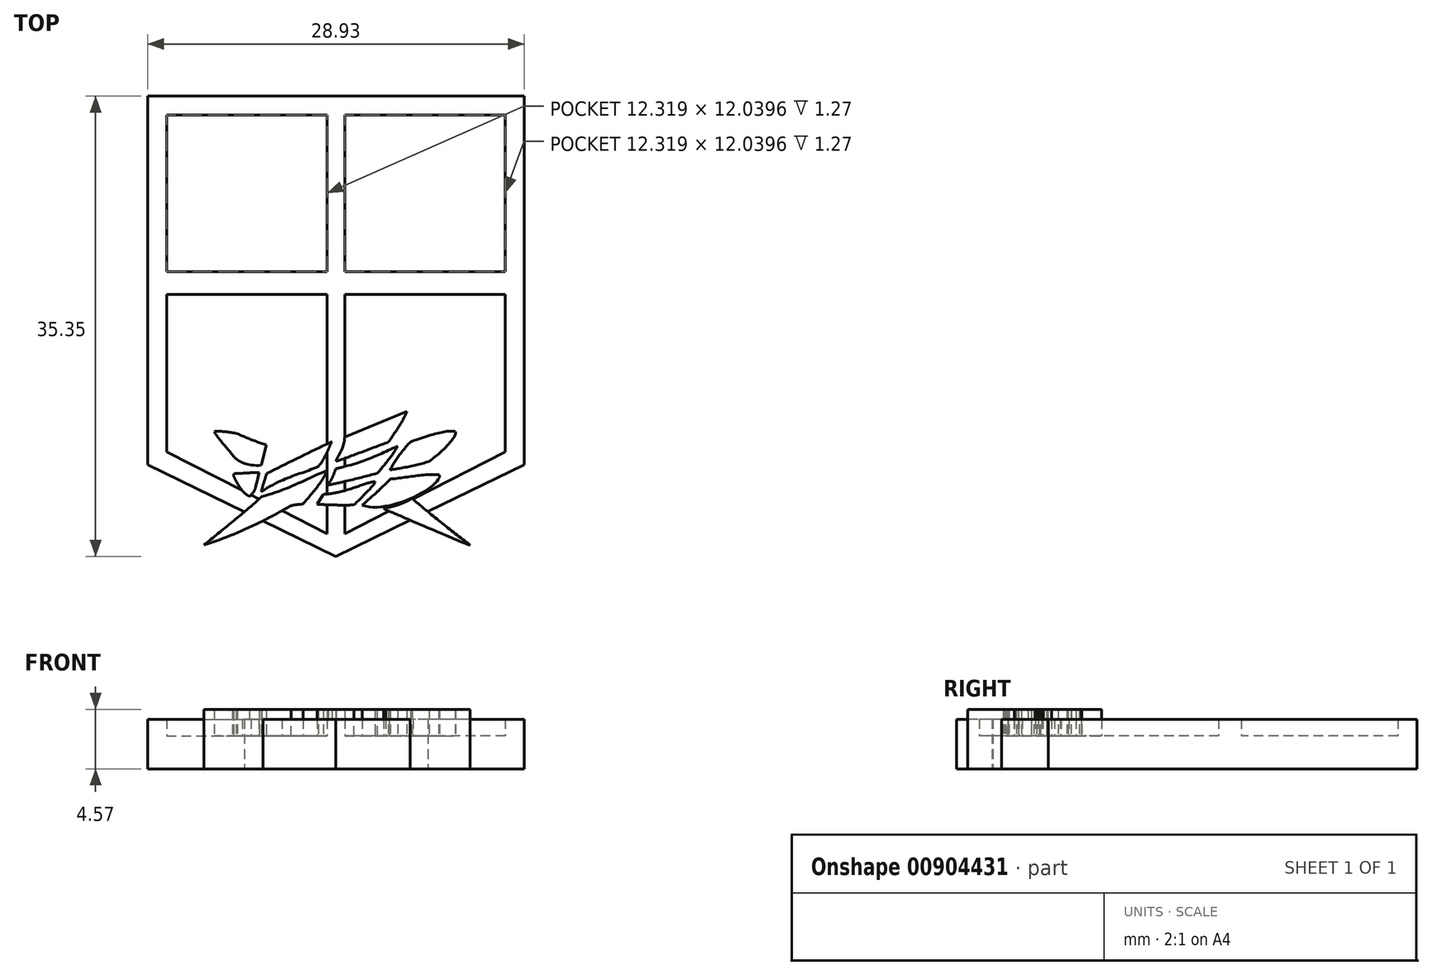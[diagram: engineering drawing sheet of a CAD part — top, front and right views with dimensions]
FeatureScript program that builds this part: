
annotation { "Feature Type Name" : "Feature", "Feature Type Description" : "" }
export const myFeature = defineFeature(function(context is Context, id is Id, definition is map)
    precondition{}
    {
        {
            var Q0;
            Q0=qCreatedBy(makeId("Top.planeOp"),FACE);
            var sketch = newSketch(context, id + "F0", { "sketchPlane" : qUnion([Q0])});
            skLineSegment(sketch, "E0", {"start": v(1.06, 6.16) * mm, "end": v(1.06, 44.26) * mm});
            skLineSegment(sketch, "E1", {"start": v(-13.4, 41.58) * mm, "end": v(-13.4, 13.28) * mm});
            skLineSegment(sketch, "E2", {"start": v(-13.4, 13.28) * mm, "end": v(1.06, 6.23) * mm});
            skLineSegment(sketch, "E3", {"start": v(-13.4, 41.58) * mm, "end": v(1.06, 41.58) * mm});
            skLineSegment(sketch, "E4", {"start": v(-11.95, 28.1) * mm, "end": v(0.37, 28.1) * mm});
            skLineSegment(sketch, "E5", {"start": v(0.37, 28.1) * mm, "end": v(0.37, 40.14) * mm});
            skLineSegment(sketch, "E6", {"start": v(0.37, 40.14) * mm, "end": v(-11.95, 40.14) * mm});
            skLineSegment(sketch, "E7", {"start": v(-11.95, 40.14) * mm, "end": v(-11.95, 28.1) * mm});
            skLineSegment(sketch, "E8", {"start": v(-11.95, 26.36) * mm, "end": v(0.37, 26.36) * mm});
            skLineSegment(sketch, "E9", {"start": v(-11.95, 26.36) * mm, "end": v(-11.95, 14.25) * mm});
            skLineSegment(sketch, "E10", {"start": v(-11.95, 14.25) * mm, "end": v(0.37, 7.97) * mm});
            skLineSegment(sketch, "E11", {"start": v(0.37, 26.36) * mm, "end": v(0.37, 7.97) * mm});
            skLineSegment(sketch, "E12.MirrorCS", {"start": v(14.08, 26.36) * mm, "end": v(1.76, 26.36) * mm});
            skLineSegment(sketch, "E13.MirrorCS", {"start": v(14.08, 26.36) * mm, "end": v(14.08, 14.25) * mm});
            skLineSegment(sketch, "E14.MirrorCS", {"start": v(14.08, 14.25) * mm, "end": v(1.76, 7.97) * mm});
            skLineSegment(sketch, "E15.MirrorCS", {"start": v(1.76, 26.36) * mm, "end": v(1.76, 7.97) * mm});
            skLineSegment(sketch, "E16.MirrorCS", {"start": v(1.76, 28.1) * mm, "end": v(1.76, 40.14) * mm});
            skLineSegment(sketch, "E17.MirrorCS", {"start": v(14.08, 40.14) * mm, "end": v(14.08, 28.1) * mm});
            skLineSegment(sketch, "E18.MirrorCS", {"start": v(14.08, 28.1) * mm, "end": v(1.76, 28.1) * mm});
            skLineSegment(sketch, "E19.MirrorCS", {"start": v(1.76, 40.14) * mm, "end": v(14.08, 40.14) * mm});
            skLineSegment(sketch, "E20.MirrorCS", {"start": v(15.53, 41.58) * mm, "end": v(1.06, 41.58) * mm});
            skLineSegment(sketch, "E21.MirrorCS", {"start": v(15.53, 41.58) * mm, "end": v(15.53, 13.28) * mm});
            skLineSegment(sketch, "E22.MirrorCS", {"start": v(15.53, 13.28) * mm, "end": v(1.06, 6.23) * mm});
            skFitSpline(sketch, "E23", {"points": [v(-4.64, 10.81) * mm, v(-9.06, 7.1) * mm], "startDerivative": vector(-4.08, -3.8) * mm, "endDerivative": vector(-4.43, -3.76) * mm});
            skFitSpline(sketch, "E24", {"points": [v(-9.06, 7.1) * mm, v(-2.38, 10.11) * mm], "startDerivative": vector(9.26, 3) * mm, "endDerivative": vector(4.95, 2.67) * mm});
            skFitSpline(sketch, "E25", {"points": [v(-2.38, 10.11) * mm, v(-1.47, 10.25) * mm], "startDerivative": vector(0.83, 0.32) * mm, "endDerivative": vector(0.9, 0.14) * mm});
            skFitSpline(sketch, "E26", {"points": [v(0.37, 12.77) * mm, v(-1.47, 10.25) * mm], "startDerivative": vector(-1.12, -2.58) * mm, "endDerivative": vector(-1.78, -2.06) * mm});
            skFitSpline(sketch, "E27", {"points": [v(0.37, 12.82) * mm, v(-4.64, 10.81) * mm], "startDerivative": vector(-5.01, -2) * mm, "endDerivative": vector(-6.37, -1.72) * mm});
            skFitSpline(sketch, "E28", {"points": [v(4.9, 9.8) * mm, v(11.38, 7.08) * mm], "startDerivative": vector(6.47, -2.73) * mm, "endDerivative": vector(1.76, -0.58) * mm});
            skFitSpline(sketch, "E29", {"points": [v(4.75, 9.93) * mm, v(4.9, 9.8) * mm], "startDerivative": vector(0.07, -0.18) * mm, "endDerivative": vector(0.18, -0.09) * mm});
            skFitSpline(sketch, "E30", {"points": [v(11.38, 7.08) * mm, v(6.92, 10.68) * mm], "startDerivative": vector(-4.53, 3.54) * mm, "endDerivative": vector(-4.26, 3.7) * mm});
            skFitSpline(sketch, "E31", {"points": [v(6.92, 10.68) * mm, v(4.75, 9.93) * mm], "startDerivative": vector(-1.87, -0.96) * mm, "endDerivative": vector(-3.66, -0.55) * mm});
            skFitSpline(sketch, "E32", {"points": [v(0.09, 10.99) * mm, v(4.08, 11.96) * mm], "startDerivative": vector(5.72, 0.35) * mm, "endDerivative": vector(2.47, 0.08) * mm});
            skFitSpline(sketch, "E33", {"points": [v(4.08, 11.96) * mm, v(2.45, 10.17) * mm], "startDerivative": vector(0.16, -0.43) * mm, "endDerivative": vector(-1.8, -1.78) * mm});
            skFitSpline(sketch, "E34", {"points": [v(2.45, 10.17) * mm, v(-0.38, 10.23) * mm], "startDerivative": vector(-2.79, -0.04) * mm, "endDerivative": vector(-2.94, 0.22) * mm});
            skFitSpline(sketch, "E35", {"points": [v(-0.38, 10.23) * mm, v(0.09, 10.99) * mm], "startDerivative": vector(0.46, 0.76) * mm, "endDerivative": vector(0.46, 0.76) * mm});
            skFitSpline(sketch, "E36", {"points": [v(5.26, 12.17) * mm, v(3.08, 10.15) * mm], "startDerivative": vector(-2.05, -2.08) * mm, "endDerivative": vector(-2.26, -1.98) * mm});
            skFitSpline(sketch, "E37", {"points": [v(3.08, 10.15) * mm, v(9, 12.28) * mm], "startDerivative": vector(5.82, -2.02) * mm, "endDerivative": vector(1.16, 2.93) * mm});
            skFitSpline(sketch, "E38", {"points": [v(9, 12.28) * mm, v(8.97, 12.5) * mm], "startDerivative": vector(0.06, 0.33) * mm, "endDerivative": vector(-0.17, 0.25) * mm});
            skFitSpline(sketch, "E39", {"points": [v(8.97, 12.5) * mm, v(5.26, 12.17) * mm], "startDerivative": vector(-3.8, 0.2) * mm, "endDerivative": vector(-3.7, -0.3) * mm});
            skFitSpline(sketch, "E40", {"points": [v(1.04, 12.95) * mm, v(0.5, 11.72) * mm], "startDerivative": vector(-0.31, -1.27) * mm, "endDerivative": vector(-0.75, -1.39) * mm});
            skFitSpline(sketch, "E41", {"points": [v(0.5, 11.72) * mm, v(4.26, 12.62) * mm], "startDerivative": vector(0.28, -0.12) * mm, "endDerivative": vector(3.72, 1.03) * mm});
            skFitSpline(sketch, "E42", {"points": [v(4.26, 12.62) * mm, v(5.81, 14.7) * mm], "startDerivative": vector(1.64, 2) * mm, "endDerivative": vector(1.44, 2.47) * mm});
            skFitSpline(sketch, "E43", {"points": [v(5.81, 14.7) * mm, v(1.04, 12.95) * mm], "startDerivative": vector(-5.12, -2.36) * mm, "endDerivative": vector(-6.9, -1.61) * mm});
            skFitSpline(sketch, "E44", {"points": [v(-4.82, 12.65) * mm, v(-5.57, 10.83) * mm], "startDerivative": vector(-1.33, -4.72) * mm, "endDerivative": vector(-1.62, -1.8) * mm});
            skFitSpline(sketch, "E45", {"points": [v(-5.57, 10.83) * mm, v(-6.8, 12.4) * mm], "startDerivative": vector(-2.19, 1.15) * mm, "endDerivative": vector(-0.4, 0.82) * mm});
            skFitSpline(sketch, "E46", {"points": [v(-6.8, 12.4) * mm, v(-6.6, 12.6) * mm], "startDerivative": vector(-0.17, 0.4) * mm, "endDerivative": vector(0.28, -0.03) * mm});
            skFitSpline(sketch, "E47", {"points": [v(-6.6, 12.6) * mm, v(-4.82, 12.65) * mm], "startDerivative": vector(3.8, 0.1) * mm, "endDerivative": vector(0.27, -0.15) * mm});
            skFitSpline(sketch, "E48", {"points": [v(5.21, 12.87) * mm, v(6.8, 15.01) * mm], "startDerivative": vector(1.32, 2.27) * mm, "endDerivative": vector(1.98, 2) * mm});
            skFitSpline(sketch, "E49", {"points": [v(6.8, 15.01) * mm, v(10.23, 15.81) * mm], "startDerivative": vector(4.76, 1.85) * mm, "endDerivative": vector(1.34, -0.46) * mm});
            skFitSpline(sketch, "E50", {"points": [v(5.21, 12.87) * mm, v(8.22, 13.53) * mm], "startDerivative": vector(2.8, 0.45) * mm, "endDerivative": vector(2.88, 1.03) * mm});
            skFitSpline(sketch, "E51", {"points": [v(8.22, 13.53) * mm, v(10.23, 15.81) * mm], "startDerivative": vector(0.67, 0.26) * mm, "endDerivative": vector(-0.9, 1.27) * mm});
            skFitSpline(sketch, "E52", {"points": [v(-4.26, 12.59) * mm, v(0.75, 15.04) * mm], "startDerivative": vector(4.98, 2.48) * mm, "endDerivative": vector(5.02, 2.41) * mm});
            skFitSpline(sketch, "E53", {"points": [v(0.75, 15.04) * mm, v(-0.28, 13.13) * mm], "startDerivative": vector(-0.88, -1.85) * mm, "endDerivative": vector(-1.56, -1.86) * mm});
            skFitSpline(sketch, "E54", {"points": [v(-0.28, 13.13) * mm, v(-4.67, 11.2) * mm], "startDerivative": vector(-4.4, -1.94) * mm, "endDerivative": vector(-5.42, -3.53) * mm});
            skFitSpline(sketch, "E55", {"points": [v(-4.67, 11.2) * mm, v(-4.26, 12.59) * mm], "startDerivative": vector(0.35, 1.39) * mm, "endDerivative": vector(0.43, 1.4) * mm});
            skFitSpline(sketch, "E56", {"points": [v(1.75, 15.4) * mm, v(6.53, 17.36) * mm], "startDerivative": vector(4.78, 1.96) * mm, "endDerivative": vector(4.78, 1.96) * mm});
            skFitSpline(sketch, "E57", {"points": [v(6.53, 17.36) * mm, v(5.1, 15) * mm], "startDerivative": vector(-1.06, -2.45) * mm, "endDerivative": vector(-1.56, -2.27) * mm});
            skFitSpline(sketch, "E58", {"points": [v(5.1, 15) * mm, v(1.07, 13.54) * mm], "startDerivative": vector(-4.03, -1.47) * mm, "endDerivative": vector(-0.26, 0.09) * mm});
            skFitSpline(sketch, "E59", {"points": [v(1.07, 13.54) * mm, v(1.75, 15.4) * mm], "startDerivative": vector(0.27, 1.25) * mm, "endDerivative": vector(0.4, 3.51) * mm});
            skFitSpline(sketch, "E60", {"points": [v(-8.27, 15.8) * mm, v(-6.88, 14.02) * mm], "startDerivative": vector(0, -0.57) * mm, "endDerivative": vector(1.37, -1.8) * mm});
            skFitSpline(sketch, "E61", {"points": [v(-6.88, 14.02) * mm, v(-4.65, 13.23) * mm], "startDerivative": vector(0.3, -0.28) * mm, "endDerivative": vector(4.86, 0.4) * mm});
            skFitSpline(sketch, "E62", {"points": [v(-4.65, 13.23) * mm, v(-4.28, 14.79) * mm], "startDerivative": vector(0.38, 1.56) * mm, "endDerivative": vector(0.38, 1.56) * mm});
            skFitSpline(sketch, "E63", {"points": [v(-4.28, 14.79) * mm, v(-6.51, 15.65) * mm], "startDerivative": vector(-2.37, 0.7) * mm, "endDerivative": vector(-2.1, 0.9) * mm});
            skFitSpline(sketch, "E64", {"points": [v(-6.51, 15.65) * mm, v(-8.27, 15.8) * mm], "startDerivative": vector(-2.53, 0.5) * mm, "endDerivative": vector(-0.34, -0.26) * mm});
            skLineSegment(sketch, "E65", {"start": v(-4.04, 15.96) * mm, "end": v(-4.15, 15.37) * mm});
            skSolve(sketch);
        }
        {
            var Q0;
            Q0=makeQuery(id+"F0.imprint","IMPRINT",FACE,{"disambiguationData":[TD([[makeQuery(id+"F0.imprint","IMPRINT",EDGE,{"derivedFrom":sQuery(id+"F0.wireOp",EDGE,"E12.MirrorCS")}),-1.0]])]});
            var Q1;
            Q1=makeQuery(id+"F0.imprint","IMPRINT",FACE,{"disambiguationData":[TD([[makeQuery(id+"F0.imprint","IMPRINT",EDGE,{"derivedFrom":sQuery(id+"F0.wireOp",EDGE,"E1")}),1.0]])]});
            var Q2;
            {var subQ0=sQuery(id+"F0.wireOp",EDGE,"E11");var subQ1=sQuery(id+"F0.wireOp",EDGE,"E10");var subQ2=makeQuery(id+"F0.imprint","INTERSECT",VERTEX,{"derivedFrom":[subQ1,subQ0]});Q2=makeQuery(id+"F0.imprint","IMPRINT",FACE,{"disambiguationData":[TD([[makeQuery(id+"F0.imprint","IMPRINT",EDGE,{"disambiguationData":[TD([[subQ2,1.0]])],"derivedFrom":subQ1}),-1.0]])]});}
            var Q3;
            {var subQ5=sQuery(id+"F0.wireOp",EDGE,"E14.MirrorCS");var subQ7=sQuery(id+"F0.wireOp",EDGE,"E15.MirrorCS");var subQ8=makeQuery(id+"F0.imprint","INTERSECT",VERTEX,{"derivedFrom":[subQ5,subQ7]});Q3=makeQuery(id+"F0.imprint","IMPRINT",FACE,{"disambiguationData":[TD([[makeQuery(id+"F0.imprint","IMPRINT",EDGE,{"disambiguationData":[TD([[subQ8,1.0]])],"derivedFrom":subQ5}),1.0]])]});}
            var Q4;
            {var subQ0=sQuery(id+"F0.wireOp",EDGE,"E32");var subQ1=sQuery(id+"F0.wireOp",EDGE,"E0");var subQ2=makeQuery(id+"F0.imprint","INTERSECT",VERTEX,{"derivedFrom":[subQ1,subQ0]});Q4=makeQuery(id+"F0.imprint","IMPRINT",FACE,{"disambiguationData":[TD([[makeQuery(id+"F0.imprint","IMPRINT",EDGE,{"disambiguationData":[TD([[subQ2,-1.0]])],"derivedFrom":subQ1}),-1.0]])]});}
            extrude(context, id + "F1", {"entities" : qUnion([Q0, Q1, Q2, Q3, Q4]), "flatOperationType" : FlatOperationType.REMOVE, "depth" : 3.8 * mm, "offsetDistance" : 25.4 * mm, "domain" : OperationDomain.MODEL});
        }
        {
            var Q0;
            Q0=makeQuery(id+"F0.imprint","IMPRINT",FACE,{"disambiguationData":[TD([[makeQuery(id+"F0.imprint","IMPRINT",EDGE,{"derivedFrom":sQuery(id+"F0.wireOp",EDGE,"E4")}),1.0]])]});
            var Q1;
            Q1=makeQuery(id+"F0.imprint","IMPRINT",FACE,{"disambiguationData":[TD([[makeQuery(id+"F0.imprint","IMPRINT",EDGE,{"derivedFrom":sQuery(id+"F0.wireOp",EDGE,"E8")}),-1.0]])]});
            var Q2;
            Q2=makeQuery(id+"F0.imprint","IMPRINT",FACE,{"disambiguationData":[TD([[makeQuery(id+"F0.imprint","IMPRINT",EDGE,{"derivedFrom":sQuery(id+"F0.wireOp",EDGE,"E12.MirrorCS")}),1.0]])]});
            var Q3;
            Q3=makeQuery(id+"F0.imprint","IMPRINT",FACE,{"disambiguationData":[TD([[makeQuery(id+"F0.imprint","IMPRINT",EDGE,{"derivedFrom":sQuery(id+"F0.wireOp",EDGE,"E16.MirrorCS")}),-1.0]])]});
            var Q4;
            {var subQ4=sQuery(id+"F0.wireOp",EDGE,"E25");Q4=makeQuery(id+"F0.imprint","IMPRINT",FACE,{"disambiguationData":[TD([[makeQuery(id+"F0.imprint","IMPRINT",EDGE,{"derivedFrom":subQ4}),-1.0]])]});}
            extrude(context, id + "F2", {"entities" : qUnion([Q0, Q1, Q2, Q3, Q4]), "operationType" : NewBodyOperationType.ADD, "flatOperationType" : FlatOperationType.REMOVE, "depth" : 2.54 * mm, "offsetDistance" : 25.4 * mm, "domain" : OperationDomain.MODEL});
        }
        {
            var Q0;
            {var subQ0=sQuery(id+"F0.wireOp",EDGE,"E25");Q0=makeQuery(id+"F0.imprint","IMPRINT",FACE,{"disambiguationData":[TD([[makeQuery(id+"F0.imprint","IMPRINT",EDGE,{"derivedFrom":subQ0}),1.0]])]});}
            var Q1;
            {var subQ0=sQuery(id+"F0.wireOp",EDGE,"E23");var subQ1=sQuery(id+"F0.wireOp",EDGE,"E2");var subQ2=makeQuery(id+"F0.imprint","INTERSECT",VERTEX,{"derivedFrom":[subQ1,subQ0]});Q1=makeQuery(id+"F0.imprint","IMPRINT",FACE,{"disambiguationData":[TD([[makeQuery(id+"F0.imprint","IMPRINT",EDGE,{"disambiguationData":[TD([[subQ2,-1.0]])],"derivedFrom":subQ1}),1.0]])]});}
            var Q2;
            {var subQ0=sQuery(id+"F0.wireOp",EDGE,"E23");var subQ1=sQuery(id+"F0.wireOp",EDGE,"E2");var subQ2=makeQuery(id+"F0.imprint","INTERSECT",VERTEX,{"derivedFrom":[subQ1,subQ0]});Q2=makeQuery(id+"F0.imprint","IMPRINT",FACE,{"disambiguationData":[TD([[makeQuery(id+"F0.imprint","IMPRINT",EDGE,{"disambiguationData":[TD([[subQ2,-1.0]])],"derivedFrom":subQ1}),-1.0]])]});}
            var Q3;
            {var subQ0=sQuery(id+"F0.wireOp",EDGE,"E30");var subQ1=sQuery(id+"F0.wireOp",EDGE,"E14.MirrorCS");var subQ2=makeQuery(id+"F0.imprint","INTERSECT",VERTEX,{"derivedFrom":[subQ1,subQ0]});Q3=makeQuery(id+"F0.imprint","IMPRINT",FACE,{"disambiguationData":[TD([[makeQuery(id+"F0.imprint","IMPRINT",EDGE,{"disambiguationData":[TD([[subQ2,-1.0]])],"derivedFrom":subQ1}),1.0]])]});}
            var Q4;
            {var subQ0=sQuery(id+"F0.wireOp",EDGE,"E30");var subQ1=sQuery(id+"F0.wireOp",EDGE,"E22.MirrorCS");var subQ2=makeQuery(id+"F0.imprint","INTERSECT",VERTEX,{"derivedFrom":[subQ1,subQ0]});Q4=makeQuery(id+"F0.imprint","IMPRINT",FACE,{"disambiguationData":[TD([[makeQuery(id+"F0.imprint","IMPRINT",EDGE,{"disambiguationData":[TD([[subQ2,-1.0]])],"derivedFrom":subQ1}),1.0]])]});}
            var Q5;
            {var subQ4=sQuery(id+"F0.wireOp",EDGE,"E29");Q5=makeQuery(id+"F0.imprint","IMPRINT",FACE,{"disambiguationData":[TD([[makeQuery(id+"F0.imprint","IMPRINT",EDGE,{"derivedFrom":subQ4}),1.0]])]});}
            var Q6;
            {var subQ5=sQuery(id+"F0.wireOp",EDGE,"E33");Q6=makeQuery(id+"F0.imprint","IMPRINT",FACE,{"disambiguationData":[TD([[makeQuery(id+"F0.imprint","IMPRINT",EDGE,{"derivedFrom":subQ5}),-1.0]])]});}
            var Q7;
            {var subQ0=sQuery(id+"F0.wireOp",EDGE,"E34");var subQ1=sQuery(id+"F0.wireOp",EDGE,"E0");var subQ2=makeQuery(id+"F0.imprint","INTERSECT",VERTEX,{"derivedFrom":[subQ1,subQ0]});Q7=makeQuery(id+"F0.imprint","IMPRINT",FACE,{"disambiguationData":[TD([[makeQuery(id+"F0.imprint","IMPRINT",EDGE,{"disambiguationData":[TD([[subQ2,-1.0]])],"derivedFrom":subQ1}),-1.0]])]});}
            var Q8;
            {var subQ0=sQuery(id+"F0.wireOp",EDGE,"E34");var subQ1=sQuery(id+"F0.wireOp",EDGE,"E0");var subQ2=makeQuery(id+"F0.imprint","INTERSECT",VERTEX,{"derivedFrom":[subQ1,subQ0]});Q8=makeQuery(id+"F0.imprint","IMPRINT",FACE,{"disambiguationData":[TD([[makeQuery(id+"F0.imprint","IMPRINT",EDGE,{"disambiguationData":[TD([[subQ2,-1.0]])],"derivedFrom":subQ1}),1.0]])]});}
            var Q9;
            {var subQ5=sQuery(id+"F0.wireOp",EDGE,"E35");Q9=makeQuery(id+"F0.imprint","IMPRINT",FACE,{"disambiguationData":[TD([[makeQuery(id+"F0.imprint","IMPRINT",EDGE,{"derivedFrom":subQ5}),-1.0]])]});}
            var Q10;
            Q10=makeQuery(id+"F0.imprint","IMPRINT",FACE,{"disambiguationData":[TD([[makeQuery(id+"F0.imprint","IMPRINT",EDGE,{"derivedFrom":sQuery(id+"F0.wireOp",EDGE,"E36")}),1.0]])]});
            var Q11;
            {var subQ5=sQuery(id+"F0.wireOp",EDGE,"E42");Q11=makeQuery(id+"F0.imprint","IMPRINT",FACE,{"disambiguationData":[TD([[makeQuery(id+"F0.imprint","IMPRINT",EDGE,{"derivedFrom":subQ5}),1.0]])]});}
            var Q12;
            {var subQ0=sQuery(id+"F0.wireOp",EDGE,"E41");var subQ1=sQuery(id+"F0.wireOp",EDGE,"E0");var subQ2=makeQuery(id+"F0.imprint","INTERSECT",VERTEX,{"derivedFrom":[subQ1,subQ0]});Q12=makeQuery(id+"F0.imprint","IMPRINT",FACE,{"disambiguationData":[TD([[makeQuery(id+"F0.imprint","IMPRINT",EDGE,{"disambiguationData":[TD([[subQ2,-1.0]])],"derivedFrom":subQ1}),-1.0]])]});}
            var Q13;
            {var subQ5=sQuery(id+"F0.wireOp",EDGE,"E40");Q13=makeQuery(id+"F0.imprint","IMPRINT",FACE,{"disambiguationData":[TD([[makeQuery(id+"F0.imprint","IMPRINT",EDGE,{"derivedFrom":subQ5}),1.0]])]});}
            var Q14;
            {var subQ0=sQuery(id+"F0.wireOp",EDGE,"E46");Q14=makeQuery(id+"F0.imprint","IMPRINT",FACE,{"disambiguationData":[TD([[makeQuery(id+"F0.imprint","IMPRINT",EDGE,{"derivedFrom":subQ0}),-1.0]])]});}
            var Q15;
            {var subQ0=sQuery(id+"F0.wireOp",EDGE,"E45");var subQ1=sQuery(id+"F0.wireOp",EDGE,"E10");var subQ2=makeQuery(id+"F0.imprint","INTERSECT",VERTEX,{"derivedFrom":[subQ1,subQ0]});Q15=makeQuery(id+"F0.imprint","IMPRINT",FACE,{"disambiguationData":[TD([[makeQuery(id+"F0.imprint","IMPRINT",EDGE,{"disambiguationData":[TD([[subQ2,-1.0]])],"derivedFrom":subQ1}),-1.0]])]});}
            var Q16;
            Q16=makeQuery(id+"F0.imprint","IMPRINT",FACE,{"disambiguationData":[TD([[makeQuery(id+"F0.imprint","IMPRINT",EDGE,{"derivedFrom":sQuery(id+"F0.wireOp",EDGE,"E60")}),1.0]])]});
            var Q17;
            {var subQ0=sQuery(id+"F0.wireOp",EDGE,"E52");var subQ1=sQuery(id+"F0.wireOp",EDGE,"E11");var subQ2=makeQuery(id+"F0.imprint","INTERSECT",VERTEX,{"derivedFrom":[subQ1,subQ0]});Q17=makeQuery(id+"F0.imprint","IMPRINT",FACE,{"disambiguationData":[TD([[makeQuery(id+"F0.imprint","IMPRINT",EDGE,{"disambiguationData":[TD([[subQ2,-1.0]])],"derivedFrom":subQ1}),1.0]])]});}
            var Q18;
            {var subQ5=sQuery(id+"F0.wireOp",EDGE,"E57");Q18=makeQuery(id+"F0.imprint","IMPRINT",FACE,{"disambiguationData":[TD([[makeQuery(id+"F0.imprint","IMPRINT",EDGE,{"derivedFrom":subQ5}),-1.0]])]});}
            var Q19;
            {var subQ0=sQuery(id+"F0.wireOp",EDGE,"E54");Q19=makeQuery(id+"F0.imprint","IMPRINT",FACE,{"disambiguationData":[TD([[makeQuery(id+"F0.imprint","IMPRINT",EDGE,{"derivedFrom":subQ0}),-1.0]])]});}
            var Q20;
            {var subQ5=sQuery(id+"F0.wireOp",EDGE,"E59");Q20=makeQuery(id+"F0.imprint","IMPRINT",FACE,{"disambiguationData":[TD([[makeQuery(id+"F0.imprint","IMPRINT",EDGE,{"derivedFrom":subQ5}),-1.0]])]});}
            var Q21;
            Q21=makeQuery(id+"F0.imprint","IMPRINT",FACE,{"disambiguationData":[TD([[makeQuery(id+"F0.imprint","IMPRINT",EDGE,{"derivedFrom":sQuery(id+"F0.wireOp",EDGE,"E48")}),-1.0]])]});
            extrude(context, id + "F3", {"entities" : qUnion([Q0, Q1, Q2, Q3, Q4, Q5, Q6, Q7, Q8, Q9, Q10, Q11, Q12, Q13, Q14, Q15, Q16, Q17, Q18, Q19, Q20, Q21]), "operationType" : NewBodyOperationType.ADD, "depth" : 4.57 * mm, "offsetDistance" : 25.4 * mm});
        }
    });
